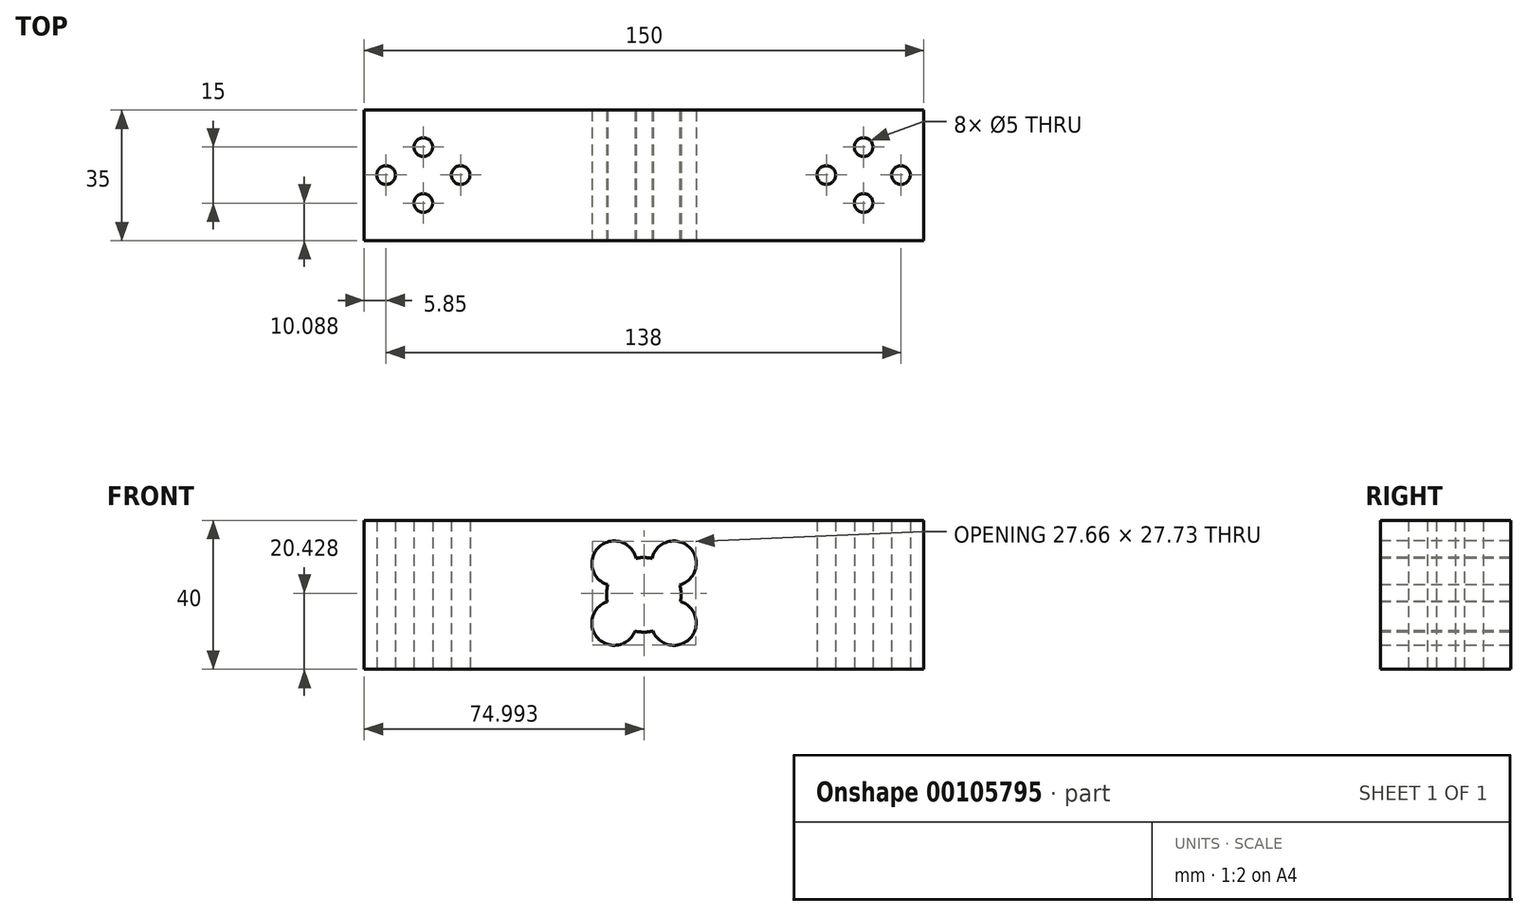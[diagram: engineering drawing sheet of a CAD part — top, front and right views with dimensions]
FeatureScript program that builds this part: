
annotation { "Feature Type Name" : "Feature", "Feature Type Description" : "" }
export const myFeature = defineFeature(function(context is Context, id is Id, definition is map)
    precondition{}
    {
        {
            var Q0;
            Q0=qCreatedBy(makeId("Top.planeOp"),FACE);
            var sketch = newSketch(context, id + "F0", { "sketchPlane" : qUnion([Q0])});
            skLineSegment(sketch, "E0.bottom", {"start": v(-74.85, 17.37) * mm, "end": v(75.15, 17.37) * mm});
            skLineSegment(sketch, "E0.top", {"start": v(-74.85, -17.63) * mm, "end": v(75.15, -17.63) * mm});
            skLineSegment(sketch, "E0.left", {"start": v(-74.85, 17.37) * mm, "end": v(-74.85, -17.63) * mm});
            skLineSegment(sketch, "E0.right", {"start": v(75.15, 17.37) * mm, "end": v(75.15, -17.63) * mm});
            skLineSegment(sketch, "E1", {"start": v(0, 17.37) * mm, "end": v(0, -38.3) * mm, "construction": true});
            skPoint(sketch, "E2", {"position": v(-69, -0.04) * mm});
            skPoint(sketch, "E3", {"position": v(-49, -0.04) * mm});
            skLineSegment(sketch, "E4", {"start": v(-69, -0.04) * mm, "end": v(-49, -0.04) * mm, "construction": true});
            skLineSegment(sketch, "E5", {"start": v(-59, -0.04) * mm, "end": v(-59, -10.45) * mm, "construction": true});
            skPoint(sketch, "E6", {"position": v(-59, -7.54) * mm});
            skPoint(sketch, "E7", {"position": v(-59, 7.46) * mm});
            skLineSegment(sketch, "E8.MirrorCS", {"start": v(69, -0.04) * mm, "end": v(49, -0.04) * mm, "construction": true});
            skPoint(sketch, "E9.MirrorP", {"position": v(59, 7.46) * mm});
            skPoint(sketch, "E10.MirrorP", {"position": v(59, -7.54) * mm});
            skPoint(sketch, "E11.MirrorP", {"position": v(69, -0.04) * mm});
            skLineSegment(sketch, "E12.MirrorCS", {"start": v(59, -0.04) * mm, "end": v(59, -10.45) * mm, "construction": true});
            skPoint(sketch, "E13.MirrorP", {"position": v(49, -0.04) * mm});
            skSolve(sketch);
        }
        {
            var Q0;
            Q0=makeQuery(id+"F0.imprint","IMPRINT",FACE,{"disambiguationData":[TD([[makeQuery(id+"F0.imprint","IMPRINT",EDGE,{"derivedFrom":sQuery(id+"F0.wireOp",EDGE,"E0.bottom")}),-1.0]])]});
            extrude(context, id + "F1", {"entities" : qUnion([Q0]), "depth" : 40 * mm});
        }
        {
            var Q0;
            Q0=sQuery(id+"F0.wireOp",VERTEX,"E7");
            var Q1;
            Q1=sQuery(id+"F0.wireOp",VERTEX,"E2");
            var Q2;
            Q2=sQuery(id+"F0.wireOp",VERTEX,"E6");
            var Q3;
            Q3=sQuery(id+"F0.wireOp",VERTEX,"E3");
            var Q4;
            Q4=sQuery(id+"F0.wireOp",VERTEX,"E13.MirrorP");
            var Q5;
            Q5=sQuery(id+"F0.wireOp",VERTEX,"E9.MirrorP");
            var Q6;
            Q6=sQuery(id+"F0.wireOp",VERTEX,"E10.MirrorP");
            var Q7;
            Q7=sQuery(id+"F0.wireOp",VERTEX,"E11.MirrorP");
            var Q8;
            Q8=makeQuery(id+"F1.opExtrude","SWEPT_BODY",BODY,{"disambiguationData":[OSD([sQuery(id+"F0.wireOp",EDGE,"E0.bottom"),sQuery(id+"F0.wireOp",EDGE,"E0.top"),sQuery(id+"F0.wireOp",EDGE,"E0.left"),sQuery(id+"F0.wireOp",EDGE,"E0.right")])]});
            hole(context, id + "F2", {"style" : HoleStyle.SIMPLE, "endStyle" : HoleEndStyle.BLIND, "oppositeDirection" : true, "holeDiameter" : 5 * mm, "holeDepth" : 50 * mm, "locations" : qUnion([Q0, Q1, Q2, Q3, Q4, Q5, Q6, Q7]), "scope" : qUnion([Q8])});
        }
        {
            var Q0;
            Q0=makeQuery(id+"F1.opExtrude","SWEPT_FACE",FACE,{"disambiguationData":[OSD([sQuery(id+"F0.wireOp",EDGE,"E0.top")])]});
            var sketch = newSketch(context, id + "F3", { "sketchPlane" : qUnion([Q0])});
            skPoint(sketch, "E14", {"position": v(8.15, 28.45) * mm});
            skPoint(sketch, "E15.0.1.0", {"position": v(8.15, 12.45) * mm});
            skPoint(sketch, "E15.1.0.0", {"position": v(-7.85, 28.45) * mm});
            skPoint(sketch, "E15.1.1.0", {"position": v(-7.85, 12.45) * mm});
            skLineSegment(sketch, "E15.direction1", {"start": v(8.15, 28.45) * mm, "end": v(-7.85, 28.45) * mm, "construction": true});
            skLineSegment(sketch, "E15.direction2", {"start": v(8.15, 28.45) * mm, "end": v(8.15, 12.45) * mm, "construction": true});
            skLineSegment(sketch, "E16", {"start": v(0.15, 40) * mm, "end": v(0, -0.73) * mm, "construction": true});
            skLineSegment(sketch, "E17", {"start": v(-74.85, 20) * mm, "end": v(75.15, 20) * mm, "construction": true});
            skPoint(sketch, "E18", {"position": v(0.08, 20) * mm});
            skSolve(sketch);
        }
        {
            var Q0;
            Q0=sQuery(id+"F3.wireOp",VERTEX,"E15.1.0.0");
            var Q1;
            Q1=sQuery(id+"F3.wireOp",VERTEX,"E14");
            var Q2;
            Q2=sQuery(id+"F3.wireOp",VERTEX,"E15.1.1.0");
            var Q3;
            Q3=sQuery(id+"F3.wireOp",VERTEX,"E15.0.1.0");
            var Q4;
            Q4=makeQuery(id+"F1.opExtrude","SWEPT_BODY",BODY,{"disambiguationData":[OSD([sQuery(id+"F0.wireOp",EDGE,"E0.bottom"),sQuery(id+"F0.wireOp",EDGE,"E0.top"),sQuery(id+"F0.wireOp",EDGE,"E0.left"),sQuery(id+"F0.wireOp",EDGE,"E0.right")])]});
            hole(context, id + "F4", {"style" : HoleStyle.SIMPLE, "endStyle" : HoleEndStyle.BLIND, "holeDiameter" : 12 * mm, "holeDepth" : 50 * mm, "locations" : qUnion([Q0, Q1, Q2, Q3]), "scope" : qUnion([Q4])});
        }
        {
            var Q0;
            Q0=sQuery(id+"F3.wireOp",VERTEX,"E18");
            var Q1;
            Q1=makeQuery(id+"F1.opExtrude","SWEPT_BODY",BODY,{"disambiguationData":[OSD([sQuery(id+"F0.wireOp",EDGE,"E0.bottom"),sQuery(id+"F0.wireOp",EDGE,"E0.top"),sQuery(id+"F0.wireOp",EDGE,"E0.left"),sQuery(id+"F0.wireOp",EDGE,"E0.right")])]});
            hole(context, id + "F5", {"style" : HoleStyle.SIMPLE, "endStyle" : HoleEndStyle.BLIND, "holeDiameter" : 20 * mm, "holeDepth" : 50 * mm, "locations" : qUnion([Q0]), "scope" : qUnion([Q1])});
        }
    });
